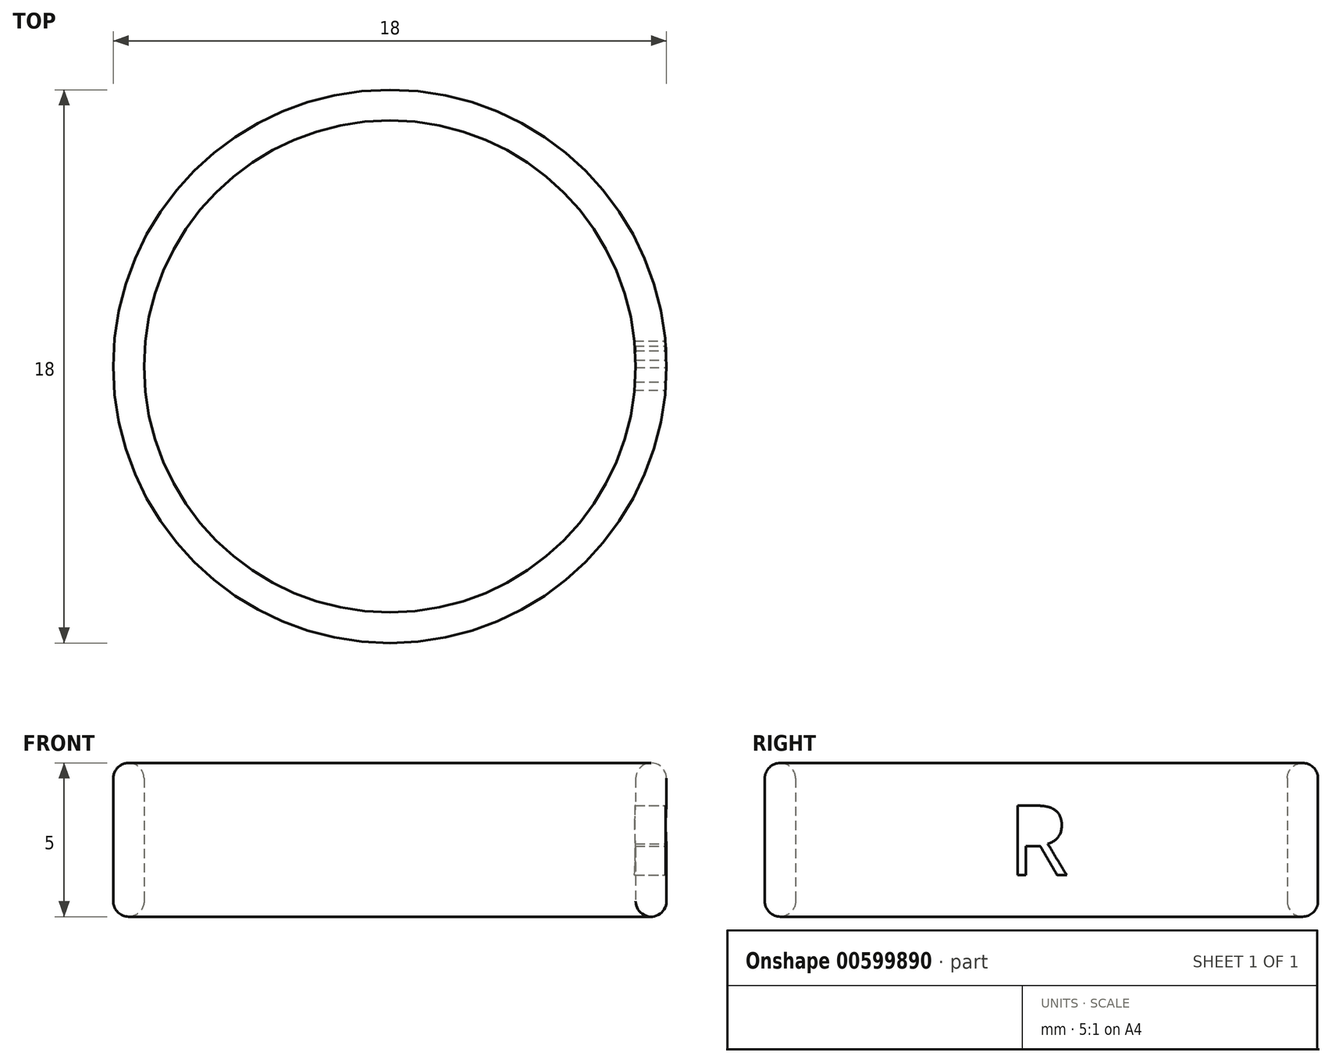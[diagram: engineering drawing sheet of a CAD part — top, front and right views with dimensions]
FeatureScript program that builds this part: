
annotation { "Feature Type Name" : "Feature", "Feature Type Description" : "" }
export const myFeature = defineFeature(function(context is Context, id is Id, definition is map)
    precondition{}
    {
        {
            var Q0;
            Q0=qCreatedBy(makeId("Top.planeOp"),FACE);
            var sketch = newSketch(context, id + "F0", { "sketchPlane" : qUnion([Q0])});
            skCircle(sketch, "E0", {"center": v(0, 0) * mm, "radius": 8 * mm});
            skCircle(sketch, "E1", {"center": v(0, 0) * mm, "radius": 9 * mm});
            skSolve(sketch);
        }
        {
            var Q0;
            Q0=makeQuery(id+"F0.imprint","IMPRINT",FACE,{"disambiguationData":[TD([[makeQuery(id+"F0.imprint","IMPRINT",EDGE,{"derivedFrom":sQuery(id+"F0.wireOp",EDGE,"E0")}),-1.0]])]});
            extrude(context, id + "F1", {"entities" : qUnion([Q0]), "depth" : 5 * mm, "offsetDistance" : 25.4 * mm});
        }
        {
            var Q0;
            Q0=makeQuery(id+"F1.opExtrude","CAP_EDGE",EDGE,{"disambiguationData":[OSD([sQuery(id+"F0.wireOp",EDGE,"E0")])],"isStart":false});
            var Q1;
            Q1=makeQuery(id+"F1.opExtrude","CAP_EDGE",EDGE,{"disambiguationData":[OSD([sQuery(id+"F0.wireOp",EDGE,"E1")])],"isStart":false});
            fillet(context, id + "F2", {"entities" : qUnion([Q0, Q1]), "radius" : .5 * mm, "tangentPropagation" : true, "allowEdgeOverflow" : false});
        }
        {
            var Q0;
            Q0=makeQuery(id+"F1.opExtrude","CAP_EDGE",EDGE,{"disambiguationData":[OSD([sQuery(id+"F0.wireOp",EDGE,"E0")])],"isStart":true});
            var Q1;
            Q1=makeQuery(id+"F1.opExtrude","CAP_EDGE",EDGE,{"disambiguationData":[OSD([sQuery(id+"F0.wireOp",EDGE,"E1")])],"isStart":true});
            fillet(context, id + "F3", {"entities" : qUnion([Q0, Q1]), "radius" : .5 * mm, "tangentPropagation" : true, "allowEdgeOverflow" : false});
        }
        {
            var Q0;
            Q0=qCreatedBy(makeId("Right.planeOp"),FACE);
            cPlane(context, id + "F4", {"entities" : qUnion([Q0]), "cplaneType" : CPlaneType.OFFSET, "offset" : 25 * mm, "width" : 150 * mm, "height" : 150 * mm});
        }
        {
            var Q0;
            Q0=qCreatedBy(id+"F4.planeOp",FACE);
            var sketch = newSketch(context, id + "F5", { "sketchPlane" : qUnion([Q0])});
            skText(sketch, "E2", { "text": "R\n", "fontName": "OpenSans-Regular.ttf"});
            skLineSegment(sketch, "E3", {"start": v(-0.6, 3.45) * mm, "end": v(-0.6, 2.43) * mm});
            skLineSegment(sketch, "E4", {"start": v(-0.6, 2.43) * mm, "end": v(0.18, 2.43) * mm});
            skLineSegment(sketch, "E5", {"start": v(0.18, 2.43) * mm, "end": v(0.48, 2.8) * mm});
            skLineSegment(sketch, "E6", {"start": v(0.48, 2.8) * mm, "end": v(0.48, 3.27) * mm});
            skLineSegment(sketch, "E7", {"start": v(0.48, 3.27) * mm, "end": v(0, 3.5) * mm});
            skLineSegment(sketch, "E8", {"start": v(0, 3.5) * mm, "end": v(-0.6, 3.45) * mm});
            const initialGuessF5  = {"E2": [-0.00108, 0.00135, 1, 0, 0.00228]};
            skSetInitialGuess(sketch, initialGuessF5);
            skSolve(sketch);
        }
        {
            var Q0;
            Q0=makeQuery(id+"F5.imprint","IMPRINT",FACE,{"disambiguationData":[TD([[makeQuery(id+"F5.imprint","IMPRINT",EDGE,{"derivedFrom":sQuery(id+"F5.wireOp",EDGE,"E2.sketch_text.stroke-11")}),-1.0]])]});
            var Q1;
            Q1=makeQuery(id+"F5.imprint","IMPRINT",FACE,{"disambiguationData":[TD([[makeQuery(id+"F5.imprint","IMPRINT",EDGE,{"derivedFrom":sQuery(id+"F5.wireOp",EDGE,"E2.sketch_text.stroke-11")}),1.0]])]});
            var Q2;
            Q2=makeQuery(id+"F5.imprint","IMPRINT",FACE,{"disambiguationData":[TD([[makeQuery(id+"F5.imprint","IMPRINT",EDGE,{"derivedFrom":sQuery(id+"F5.wireOp",EDGE,"E2.sketch_text.stroke-0")}),-1.0]])]});
            extrude(context, id + "F6", {"entities" : qUnion([Q0, Q1, Q2]), "operationType" : NewBodyOperationType.REMOVE, "oppositeDirection" : true, "depth" : 25 * mm, "offsetDistance" : 25 * mm});
        }
    });
